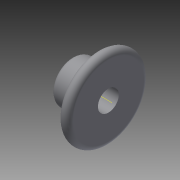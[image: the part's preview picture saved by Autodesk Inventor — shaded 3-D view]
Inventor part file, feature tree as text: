
AUTODESK INVENTOR PART (.ipt)
format: ipt  version: 2015 (Build 190159000, 159)  size: 128,000 bytes
history: native  units: mm
features: fillet x2, revolve x1, sketch x1
ambient origin geometry x8: Origin, YZ Plane, XZ Plane, XY Plane, X Axis, Y Axis, Z Axis, Center Point
bodies: Solid1 (feature_tree)
feature tree (4):
  revolve  "Revolution1"  [1 undecoded]
  fillet  "Fillet1"  Radius=2.0mm
  fillet  "Fillet2"  [1 undecoded]
  sketch  "Sketch1"  dims[d0=90.0deg d1=2.0mm d2=2.0mm]
note: 2 required parameter values undecoded (feature->parameter linkage not recoverable at this tier; creation-order binding heuristic only, values carry confidence <= 0.55)